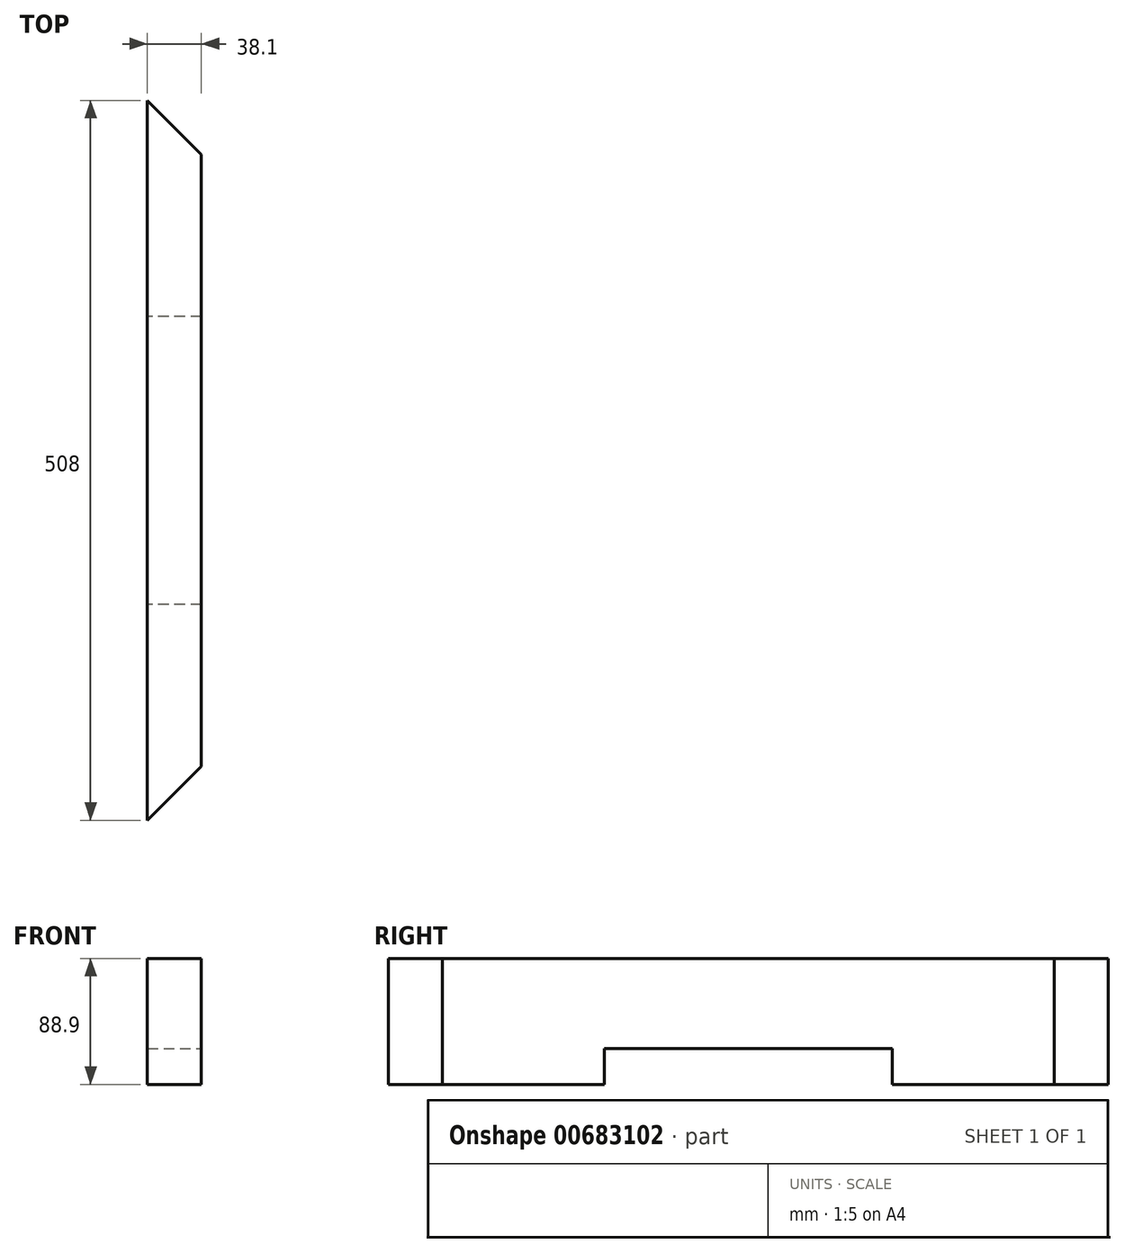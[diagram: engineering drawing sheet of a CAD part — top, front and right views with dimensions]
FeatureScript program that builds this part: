
annotation { "Feature Type Name" : "Feature", "Feature Type Description" : "" }
export const myFeature = defineFeature(function(context is Context, id is Id, definition is map)
    precondition{}
    {
        {
            var Q0;
            Q0=qCreatedBy(makeId("Top.planeOp"),FACE);
            var sketch = newSketch(context, id + "F0", { "sketchPlane" : qUnion([Q0])});
            skLineSegment(sketch, "E0.bottom", {"start": v(0, 0) * mm, "end": v(38.1, 0) * mm});
            skLineSegment(sketch, "E0.top", {"start": v(0, 508) * mm, "end": v(38.1, 508) * mm});
            skLineSegment(sketch, "E0.left", {"start": v(0, 0) * mm, "end": v(0, 508) * mm});
            skLineSegment(sketch, "E0.right", {"start": v(38.1, 0) * mm, "end": v(38.1, 508) * mm});
            skLineSegment(sketch, "E1", {"start": v(0, 508) * mm, "end": v(38.1, 469.9) * mm});
            skLineSegment(sketch, "E2", {"start": v(0, 0) * mm, "end": v(38.1, 38.1) * mm});
            skSolve(sketch);
        }
        {
            var Q0;
            Q0=makeQuery(id+"F0.imprint","IMPRINT",FACE,{"disambiguationData":[TD([[makeQuery(id+"F0.imprint","IMPRINT",EDGE,{"derivedFrom":sQuery(id+"F0.wireOp",EDGE,"E0.left")}),-1.0]])]});
            extrude(context, id + "F1", {"entities" : qUnion([Q0]), "depth" : 88.9 * mm, "offsetDistance" : 25.4 * mm});
        }
        {
            var Q0;
            Q0=makeQuery(id+"F1.opExtrude","SWEPT_FACE",FACE,{"disambiguationData":[OSD([sQuery(id+"F0.wireOp",EDGE,"E0.right")])]});
            var sketch = newSketch(context, id + "F2", { "sketchPlane" : qUnion([Q0])});
            skLineSegment(sketch, "E3.bottom", {"start": v(355.6, -25.4) * mm, "end": v(152.4, -25.4) * mm});
            skLineSegment(sketch, "E3.top", {"start": v(355.6, 25.4) * mm, "end": v(152.4, 25.4) * mm});
            skLineSegment(sketch, "E3.left", {"start": v(355.6, -25.4) * mm, "end": v(355.6, 25.4) * mm});
            skLineSegment(sketch, "E3.right", {"start": v(152.4, -25.4) * mm, "end": v(152.4, 25.4) * mm});
            skPoint(sketch, "E3.middle", {"position": v(254, 0) * mm});
            skSolve(sketch);
        }
        {
            var Q0;
            Q0 = qSketchRegion(id + "F2", true);
            extrude(context, id + "F3", {"entities" : qUnion([Q0]), "operationType" : NewBodyOperationType.REMOVE, "oppositeDirection" : true, "depth" : 72.8 * mm, "offsetDistance" : 25.4 * mm});
        }
    });
